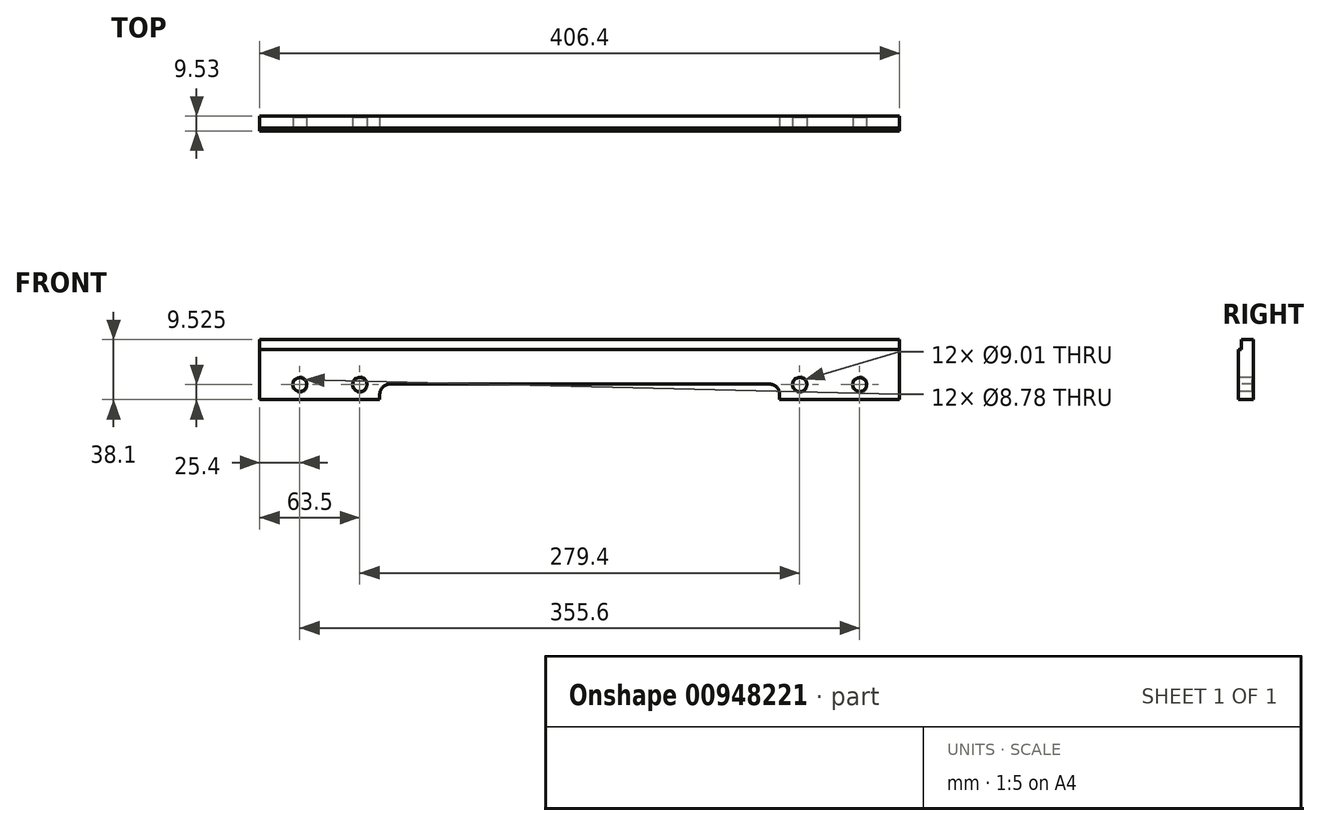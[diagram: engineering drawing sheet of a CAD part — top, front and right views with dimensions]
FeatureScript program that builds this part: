
annotation { "Feature Type Name" : "Feature", "Feature Type Description" : "" }
export const myFeature = defineFeature(function(context is Context, id is Id, definition is map)
    precondition{}
    {
        {
            var Q0;
            Q0=qCreatedBy(makeId("Front.planeOp"),FACE);
            var sketch = newSketch(context, id + "F0", { "sketchPlane" : qUnion([Q0])});
            skLineSegment(sketch, "E0", {"start": v(0, 0) * mm, "end": v(0, 524.26) * mm, "construction": true});
            skLineSegment(sketch, "E1", {"start": v(-315.37, 0) * mm, "end": v(456.8, 0) * mm, "construction": true});
            skLineSegment(sketch, "E2.bottom", {"start": v(-203.2, 19.05) * mm, "end": v(203.2, 19.05) * mm});
            skLineSegment(sketch, "E2.left", {"start": v(-203.2, 19.05) * mm, "end": v(-203.2, -19.05) * mm});
            skLineSegment(sketch, "E2.right", {"start": v(203.2, 19.05) * mm, "end": v(203.2, -19.05) * mm});
            skLineSegment(sketch, "E3.trimOffspring", {"start": v(-203.2, -19.05) * mm, "end": v(203.2, -19.05) * mm});
            skSolve(sketch);
        }
        {
            var Q0;
            Q0 = qSketchRegion(id + "F0", true);
            extrude(context, id + "F1", {"entities" : qUnion([Q0]), "depth" : 9.52 * mm, "offsetDistance" : 25.4 * mm});
        }
        {
            var Q0;
            Q0=makeQuery(id+"F1.opExtrude","CAP_FACE",FACE,{"disambiguationData":[OSD([sQuery(id+"F0.wireOp",EDGE,"E2.bottom"),sQuery(id+"F0.wireOp",EDGE,"E2.left"),sQuery(id+"F0.wireOp",EDGE,"E2.right"),sQuery(id+"F0.wireOp",EDGE,"E3.trimOffspring")])],"isStart":false});
            var sketch = newSketch(context, id + "F2", { "sketchPlane" : qUnion([Q0])});
            skLineSegment(sketch, "E4.bottom", {"start": v(-127, -19.05) * mm, "end": v(127, -19.05) * mm});
            skLineSegment(sketch, "E4.top", {"start": v(-127, -9.27) * mm, "end": v(127, -9.27) * mm});
            skLineSegment(sketch, "E4.left", {"start": v(-127, -19.05) * mm, "end": v(-127, -9.27) * mm});
            skLineSegment(sketch, "E4.right", {"start": v(127, -19.05) * mm, "end": v(127, -9.27) * mm});
            skLineSegment(sketch, "E5", {"start": v(0, 209.58) * mm, "end": v(0, -49.2) * mm, "construction": true});
            skSolve(sketch);
        }
        {
            var Q0;
            Q0 = qSketchRegion(id + "F2", true);
            extrude(context, id + "F3", {"entities" : qUnion([Q0]), "operationType" : NewBodyOperationType.REMOVE, "endBound" : BoundingType.THROUGH_ALL, "oppositeDirection" : true, "depth" : 25.4 * mm, "offsetDistance" : 25.4 * mm});
        }
        {
            var Q0;
            Q0=makeQuery(id+"F3.boolean.opBoolean","COPY",EDGE,{"derivedFrom":makeQuery(id+"F3.opExtrude","SWEPT_EDGE",EDGE,{"disambiguationData":[OSD([sQuery(id+"F2.wireOp",EDGE,"E4.top"),sQuery(id+"F2.wireOp",EDGE,"E4.left")])]})});
            var Q1;
            Q1=makeQuery(id+"F3.boolean.opBoolean","COPY",EDGE,{"derivedFrom":makeQuery(id+"F3.opExtrude","SWEPT_EDGE",EDGE,{"disambiguationData":[OSD([sQuery(id+"F2.wireOp",EDGE,"E4.top"),sQuery(id+"F2.wireOp",EDGE,"E4.right")])]})});
            fillet(context, id + "F4", {"entities" : qUnion([Q0, Q1]), "radius" : 6.35 * mm, "tangentPropagation" : true, "allowEdgeOverflow" : false});
        }
        {
            var Q0;
            Q0=makeQuery(id+"F1.opExtrude","CAP_FACE",FACE,{"disambiguationData":[OSD([sQuery(id+"F0.wireOp",EDGE,"E2.bottom"),sQuery(id+"F0.wireOp",EDGE,"E2.left"),sQuery(id+"F0.wireOp",EDGE,"E2.right"),sQuery(id+"F0.wireOp",EDGE,"E3.trimOffspring")])],"isStart":false});
            var sketch = newSketch(context, id + "F5", { "sketchPlane" : qUnion([Q0])});
            skLineSegment(sketch, "E6", {"start": v(0, 188.07) * mm, "end": v(0, -74.74) * mm, "construction": true});
            skLineSegment(sketch, "E7.bottom", {"start": v(-203.2, 19.05) * mm, "end": v(203.2, 19.05) * mm});
            skLineSegment(sketch, "E7.top", {"start": v(-203.2, 12.7) * mm, "end": v(203.2, 12.7) * mm});
            skLineSegment(sketch, "E7.left", {"start": v(-203.2, 19.05) * mm, "end": v(-203.2, 12.7) * mm});
            skLineSegment(sketch, "E7.right", {"start": v(203.2, 19.05) * mm, "end": v(203.2, 12.7) * mm});
            skSolve(sketch);
        }
        {
            var Q0;
            Q0 = qSketchRegion(id + "F5", true);
            extrude(context, id + "F6", {"entities" : qUnion([Q0]), "operationType" : NewBodyOperationType.REMOVE, "oppositeDirection" : true, "depth" : 1.78 * mm, "offsetDistance" : 25.4 * mm});
        }
        {
            var Q0;
            Q0=makeQuery(id+"F1.opExtrude","CAP_FACE",FACE,{"disambiguationData":[OSD([sQuery(id+"F0.wireOp",EDGE,"E2.bottom"),sQuery(id+"F0.wireOp",EDGE,"E2.left"),sQuery(id+"F0.wireOp",EDGE,"E2.right"),sQuery(id+"F0.wireOp",EDGE,"E3.trimOffspring")])],"isStart":false});
            var sketch = newSketch(context, id + "F7", { "sketchPlane" : qUnion([Q0])});
            skCircle(sketch, "E8", {"center": v(139.7, -9.53) * mm, "radius": 4.5 * mm});
            skCircle(sketch, "E9", {"center": v(177.8, -9.53) * mm, "radius": 4.39 * mm});
            skLineSegment(sketch, "E10", {"start": v(-203.2, -9.53) * mm, "end": v(203.2, -9.53) * mm, "construction": true});
            skLineSegment(sketch, "E11", {"start": v(0, 49.94) * mm, "end": v(0, -59.63) * mm, "construction": true});
            skCircle(sketch, "E12.MirrorC", {"center": v(-177.8, -9.53) * mm, "radius": 4.39 * mm});
            skCircle(sketch, "E13.MirrorC", {"center": v(-139.7, -9.53) * mm, "radius": 4.5 * mm});
            skSolve(sketch);
        }
        {
            var Q0;
            Q0 = qSketchRegion(id + "F7", true);
            extrude(context, id + "F8", {"entities" : qUnion([Q0]), "operationType" : NewBodyOperationType.REMOVE, "endBound" : BoundingType.THROUGH_ALL, "oppositeDirection" : true, "depth" : 25.4 * mm, "offsetDistance" : 25.4 * mm});
        }
        {
            var Q0;
            Q0=makeQuery(id+"F8.boolean.opBoolean","COPY",EDGE,{"derivedFrom":makeQuery(id+"F8.opExtrude","CAP_EDGE",EDGE,{"disambiguationData":[OSD([sQuery(id+"F7.wireOp",EDGE,"E12.MirrorC")])],"isStart":true})});
            var Q1;
            Q1=makeQuery(id+"F8.boolean.opBoolean","COPY",EDGE,{"derivedFrom":makeQuery(id+"F8.opExtrude","CAP_EDGE",EDGE,{"disambiguationData":[OSD([sQuery(id+"F7.wireOp",EDGE,"E13.MirrorC")])],"isStart":true})});
            var Q2;
            Q2=makeQuery(id+"F8.boolean.opBoolean","COPY",EDGE,{"derivedFrom":makeQuery(id+"F8.opExtrude","CAP_EDGE",EDGE,{"disambiguationData":[OSD([sQuery(id+"F7.wireOp",EDGE,"E8")])],"isStart":true})});
            var Q3;
            Q3=makeQuery(id+"F8.boolean.opBoolean","COPY",EDGE,{"derivedFrom":makeQuery(id+"F8.opExtrude","CAP_EDGE",EDGE,{"disambiguationData":[OSD([sQuery(id+"F7.wireOp",EDGE,"E9")])],"isStart":true})});
            var Q4;
            Q4=makeQuery(id+"F8.boolean.opBoolean","INTERSECT",EDGE,{"derivedFrom":[makeQuery(id+"F1.opExtrude","CAP_FACE",FACE,{"disambiguationData":[OSD([sQuery(id+"F0.wireOp",EDGE,"E2.bottom"),sQuery(id+"F0.wireOp",EDGE,"E2.left"),sQuery(id+"F0.wireOp",EDGE,"E2.right"),sQuery(id+"F0.wireOp",EDGE,"E3.trimOffspring")])],"isStart":true}),makeQuery(id+"F8.opExtrude","SWEPT_FACE",FACE,{"disambiguationData":[OSD([sQuery(id+"F7.wireOp",EDGE,"E9")])]})]});
            var Q5;
            Q5=makeQuery(id+"F8.boolean.opBoolean","INTERSECT",EDGE,{"derivedFrom":[makeQuery(id+"F1.opExtrude","CAP_FACE",FACE,{"disambiguationData":[OSD([sQuery(id+"F0.wireOp",EDGE,"E2.bottom"),sQuery(id+"F0.wireOp",EDGE,"E2.left"),sQuery(id+"F0.wireOp",EDGE,"E2.right"),sQuery(id+"F0.wireOp",EDGE,"E3.trimOffspring")])],"isStart":true}),makeQuery(id+"F8.opExtrude","SWEPT_FACE",FACE,{"disambiguationData":[OSD([sQuery(id+"F7.wireOp",EDGE,"E8")])]})]});
            var Q6;
            Q6=makeQuery(id+"F8.boolean.opBoolean","INTERSECT",EDGE,{"derivedFrom":[makeQuery(id+"F1.opExtrude","CAP_FACE",FACE,{"disambiguationData":[OSD([sQuery(id+"F0.wireOp",EDGE,"E2.bottom"),sQuery(id+"F0.wireOp",EDGE,"E2.left"),sQuery(id+"F0.wireOp",EDGE,"E2.right"),sQuery(id+"F0.wireOp",EDGE,"E3.trimOffspring")])],"isStart":true}),makeQuery(id+"F8.opExtrude","SWEPT_FACE",FACE,{"disambiguationData":[OSD([sQuery(id+"F7.wireOp",EDGE,"E13.MirrorC")])]})]});
            var Q7;
            Q7=makeQuery(id+"F8.boolean.opBoolean","INTERSECT",EDGE,{"derivedFrom":[makeQuery(id+"F1.opExtrude","CAP_FACE",FACE,{"disambiguationData":[OSD([sQuery(id+"F0.wireOp",EDGE,"E2.bottom"),sQuery(id+"F0.wireOp",EDGE,"E2.left"),sQuery(id+"F0.wireOp",EDGE,"E2.right"),sQuery(id+"F0.wireOp",EDGE,"E3.trimOffspring")])],"isStart":true}),makeQuery(id+"F8.opExtrude","SWEPT_FACE",FACE,{"disambiguationData":[OSD([sQuery(id+"F7.wireOp",EDGE,"E12.MirrorC")])]})]});
            chamfer(context, id + "F9", {"entities" : qUnion([Q0, Q1, Q2, Q3, Q4, Q5, Q6, Q7]), "width" : 0.76 * mm, "tangentPropagation" : true});
        }
    });
